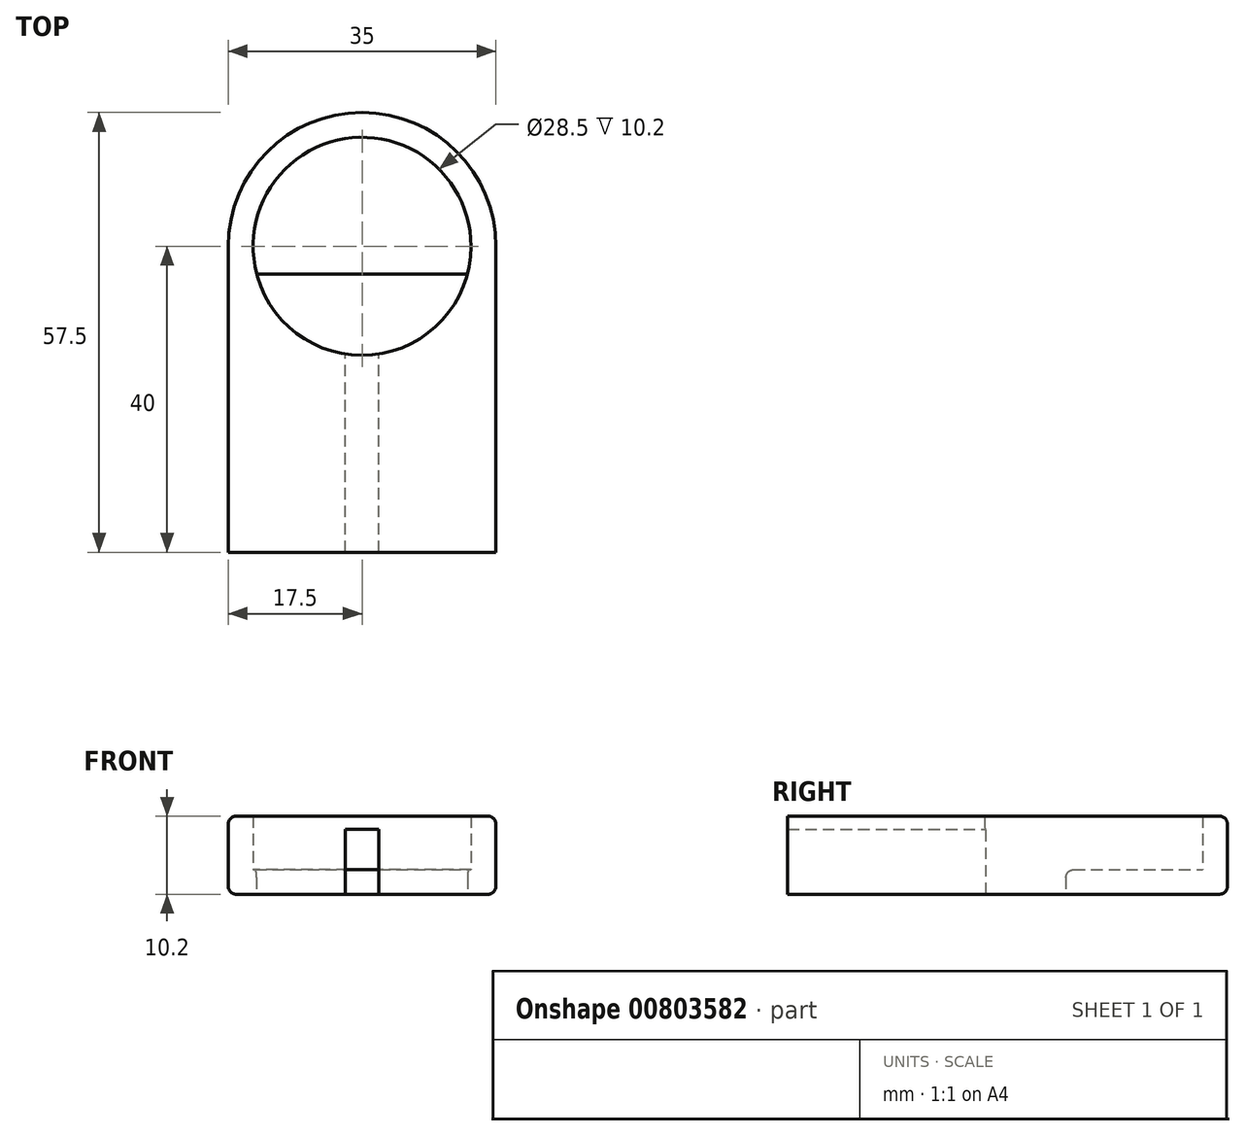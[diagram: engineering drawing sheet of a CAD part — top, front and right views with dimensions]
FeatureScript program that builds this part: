
annotation { "Feature Type Name" : "Feature", "Feature Type Description" : "" }
export const myFeature = defineFeature(function(context is Context, id is Id, definition is map)
    precondition{}
    {
        {
            var Q0;
            Q0=qCreatedBy(makeId("Top.planeOp"),FACE);
            var sketch = newSketch(context, id + "F0", { "sketchPlane" : qUnion([Q0])});
            skLineSegment(sketch, "E0.bottom", {"start": v(-17.5, -20) * mm, "end": v(17.5, -20) * mm});
            skLineSegment(sketch, "E0.top", {"start": v(-17.5, 20) * mm, "end": v(17.5, 20) * mm});
            skLineSegment(sketch, "E0.left", {"start": v(-17.5, -20) * mm, "end": v(-17.5, 20) * mm});
            skLineSegment(sketch, "E0.right", {"start": v(17.5, -20) * mm, "end": v(17.5, 20) * mm});
            skCircle(sketch, "E1", {"center": v(0, 20) * mm, "radius": 17.5 * mm});
            skSolve(sketch);
        }
        {
            var Q0;
            Q0=makeQuery(id+"F0.imprint","IMPRINT",FACE,{"disambiguationData":[TD([[makeQuery(id+"F0.imprint","IMPRINT",EDGE,{"derivedFrom":sQuery(id+"F0.wireOp",EDGE,"E0.bottom")}),1.0]])]});
            var Q1;
            {var subQ0=sQuery(id+"F0.wireOp",EDGE,"E0.top");Q1=makeQuery(id+"F0.imprint","IMPRINT",FACE,{"disambiguationData":[TD([[makeQuery(id+"F0.imprint","IMPRINT",EDGE,{"derivedFrom":subQ0}),-1.0]])]});}
            var Q2;
            {var subQ0=sQuery(id+"F0.wireOp",EDGE,"E0.top");Q2=makeQuery(id+"F0.imprint","IMPRINT",FACE,{"disambiguationData":[TD([[makeQuery(id+"F0.imprint","IMPRINT",EDGE,{"derivedFrom":subQ0}),1.0]])]});}
            extrude(context, id + "F1", {"entities" : qUnion([Q0, Q1, Q2]), "oppositeDirection" : true, "depth" : 10.2 * mm, "offsetDistance" : 25 * mm});
        }
        {
            var Q0;
            Q0=qCreatedBy(makeId("Top.planeOp"),FACE);
            var sketch = newSketch(context, id + "F2", { "sketchPlane" : qUnion([Q0])});
            skCircle(sketch, "E2", {"center": v(0, 20) * mm, "radius": 14.25 * mm});
            skSolve(sketch);
        }
        {
            var Q0;
            Q0 = qSketchRegion(id + "F2", true);
            extrude(context, id + "F3", {"entities" : qUnion([Q0]), "oppositeDirection" : true, "depth" : 7 * mm, "offsetDistance" : 25 * mm});
        }
        {
            var Q0;
            Q0=makeQuery(id+"F1.opExtrude","CAP_FACE",FACE,{"disambiguationData":[OSD([sQuery(id+"F0.wireOp",EDGE,"E0.bottom"),sQuery(id+"F0.wireOp",EDGE,"E0.left"),sQuery(id+"F0.wireOp",EDGE,"E0.right"),sQuery(id+"F0.wireOp",EDGE,"E1")])],"isStart":false});
            var sketch = newSketch(context, id + "F4", { "sketchPlane" : qUnion([Q0])});
            skLineSegment(sketch, "E3.bottom", {"start": v(-2.2, 20) * mm, "end": v(2.2, 20) * mm});
            skLineSegment(sketch, "E3.top", {"start": v(-2.2, -10) * mm, "end": v(2.2, -10) * mm});
            skLineSegment(sketch, "E3.left", {"start": v(-2.2, 20) * mm, "end": v(-2.2, -10) * mm});
            skLineSegment(sketch, "E3.right", {"start": v(2.2, 20) * mm, "end": v(2.2, -10) * mm});
            skSolve(sketch);
        }
        {
            var Q0;
            Q0 = qSketchRegion(id + "F4", true);
            extrude(context, id + "F5", {"entities" : qUnion([Q0]), "oppositeDirection" : true, "depth" : 8.5 * mm, "offsetDistance" : 25 * mm});
        }
        {
            var Q0;
            Q0=makeQuery(id+"F1.opExtrude","CAP_FACE",FACE,{"disambiguationData":[OSD([sQuery(id+"F0.wireOp",EDGE,"E0.bottom"),sQuery(id+"F0.wireOp",EDGE,"E0.left"),sQuery(id+"F0.wireOp",EDGE,"E0.right"),sQuery(id+"F0.wireOp",EDGE,"E1")])],"isStart":false});
            var sketch = newSketch(context, id + "F6", { "sketchPlane" : qUnion([Q0])});
            skArc(sketch, "E4", {"start": v(13.78, -16.38) * mm, "mid": v(0, -5.75) * mm, "end": v(-13.78, -16.38) * mm});
            skLineSegment(sketch, "E5", {"start": v(-13.78, -16.38) * mm, "end": v(13.78, -16.38) * mm});
            skSolve(sketch);
        }
        {
            var Q0;
            Q0=makeQuery(id+"F6.imprint","IMPRINT",FACE,{"disambiguationData":[TD([[makeQuery(id+"F6.imprint","IMPRINT",EDGE,{"derivedFrom":sQuery(id+"F6.wireOp",EDGE,"E4")}),1.0]])]});
            extrude(context, id + "F7", {"entities" : qUnion([Q0]), "oppositeDirection" : true, "depth" : 25 * mm, "offsetDistance" : 25 * mm});
        }
        {
            var Q0;
            Q0=makeQuery(id+"F7.opExtrude","SWEPT_BODY",BODY,{"disambiguationData":[OSD([sQuery(id+"F6.wireOp",EDGE,"E4"),sQuery(id+"F6.wireOp",EDGE,"E5")])]});
            var Q1;
            Q1=makeQuery(id+"F5.opExtrude","SWEPT_BODY",BODY,{"disambiguationData":[OSD([sQuery(id+"F4.wireOp",EDGE,"E3.bottom"),sQuery(id+"F4.wireOp",EDGE,"E3.top"),sQuery(id+"F4.wireOp",EDGE,"E3.left"),sQuery(id+"F4.wireOp",EDGE,"E3.right")])]});
            var Q2;
            Q2=makeQuery(id+"F3.opExtrude","SWEPT_BODY",BODY,{"disambiguationData":[OSD([sQuery(id+"F2.wireOp",EDGE,"E2")])]});
            var Q3;
            Q3=makeQuery(id+"F1.opExtrude","SWEPT_BODY",BODY,{"disambiguationData":[OSD([sQuery(id+"F0.wireOp",EDGE,"E0.bottom"),sQuery(id+"F0.wireOp",EDGE,"E0.left"),sQuery(id+"F0.wireOp",EDGE,"E0.right"),sQuery(id+"F0.wireOp",EDGE,"E1")])]});
            booleanBodies(context, id + "F8", {"operationType" : BooleanOperationType.SUBTRACTION, "tools" : qUnion([Q0, Q1, Q2]), "targets" : qUnion([Q3])});
        }
        {
            var Q0;
            Q0=makeQuery(id+"F1.opExtrude","CAP_EDGE",EDGE,{"disambiguationData":[OSD([sQuery(id+"F0.wireOp",EDGE,"E1")])],"isStart":true});
            var Q1;
            Q1=makeQuery(id+"F1.opExtrude","CAP_EDGE",EDGE,{"disambiguationData":[OSD([sQuery(id+"F0.wireOp",EDGE,"E1")])],"isStart":false});
            var Q2;
            Q2=makeQuery(id+"F8.opBoolean","INTERSECT",EDGE,{"derivedFrom":[makeQuery(id+"F3.opExtrude","CAP_FACE",FACE,{"disambiguationData":[OSD([sQuery(id+"F2.wireOp",EDGE,"E2")])],"isStart":false}),makeQuery(id+"F7.opExtrude","SWEPT_FACE",FACE,{"disambiguationData":[OSD([sQuery(id+"F6.wireOp",EDGE,"E5")])]})]});
            fillet(context, id + "F9", {"entities" : qUnion([Q0, Q1, Q2]), "radius" : 1 * mm, "tangentPropagation" : true, "allowEdgeOverflow" : false});
        }
    });
